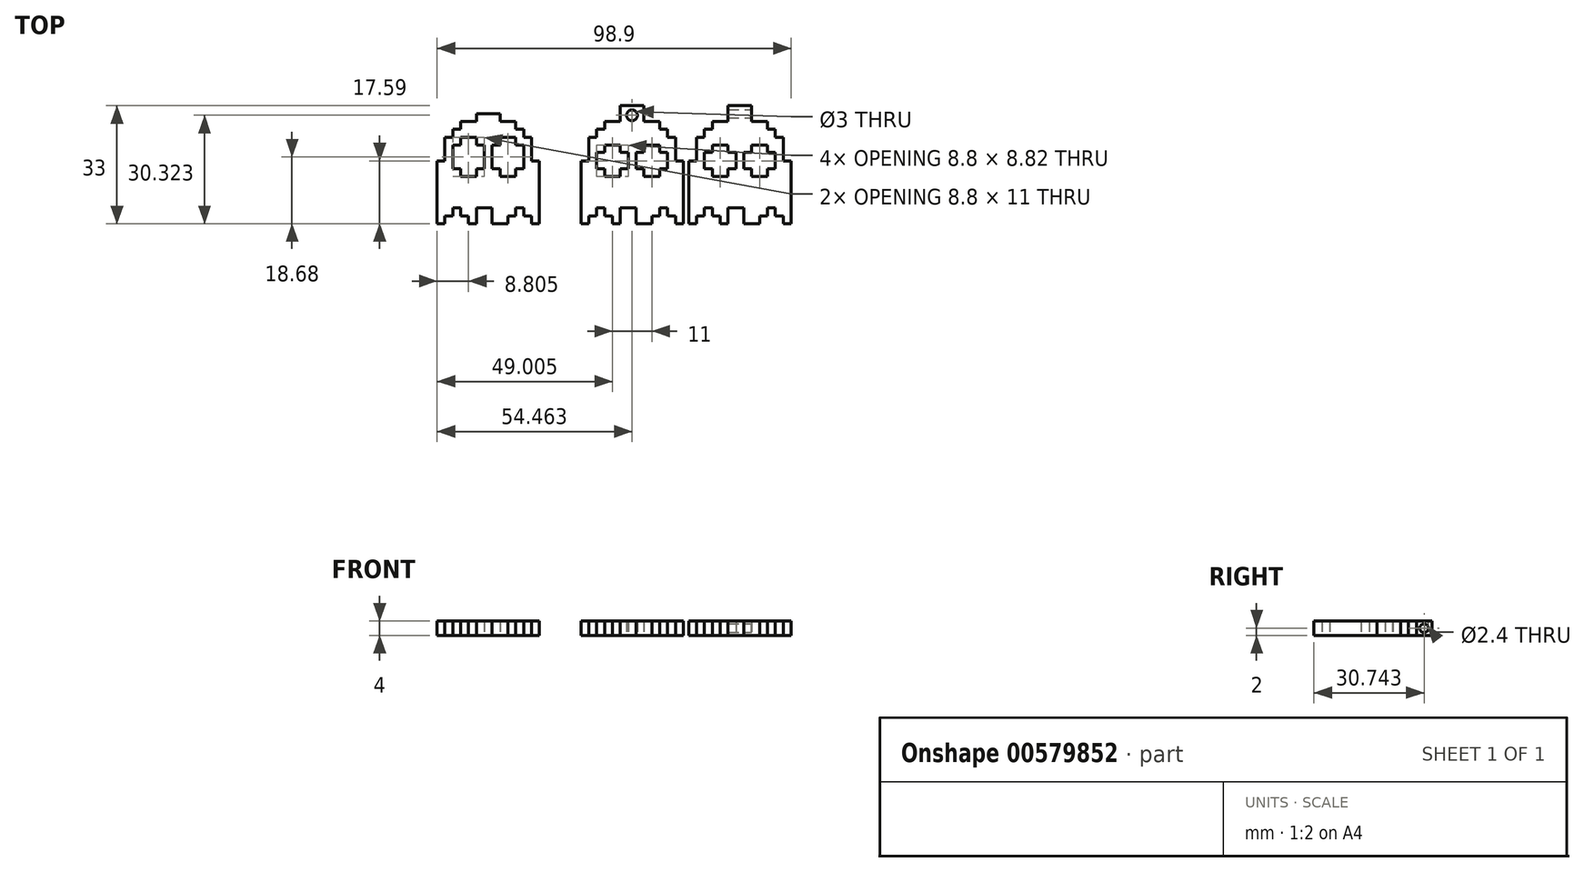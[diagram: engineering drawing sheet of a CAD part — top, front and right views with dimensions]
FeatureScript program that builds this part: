
annotation { "Feature Type Name" : "Feature", "Feature Type Description" : "" }
export const myFeature = defineFeature(function(context is Context, id is Id, definition is map)
    precondition{}
    {
        {
            var Q0;
            Q0=qCreatedBy(makeId("Top.planeOp"),FACE);
            var sketch = newSketch(context, id + "F0", { "sketchPlane" : qUnion([Q0])});
            skLineSegment(sketch, "E0.2.0.0", {"start": v(-51.84, 43.44) * mm, "end": v(-51.84, 41.24) * mm});
            skLineSegment(sketch, "E0.3.0.0", {"start": v(-49.64, 45.64) * mm, "end": v(-49.64, 43.44) * mm});
            skLineSegment(sketch, "E0.10.0.0", {"start": v(-34.24, 45.64) * mm, "end": v(-34.24, 43.44) * mm});
            skLineSegment(sketch, "E0.11.0.0", {"start": v(-32.04, 43.44) * mm, "end": v(-32.04, 41.24) * mm});
            skLineSegment(sketch, "E0.12.0.0", {"start": v(-29.84, 41.24) * mm, "end": v(-29.84, 34.64) * mm});
            skLineSegment(sketch, "E0.direction1", {"start": v(-56.24, 17.04) * mm, "end": v(-54.04, 17.04) * mm, "construction": true});
            skLineSegment(sketch, "E1.0.2.0", {"start": v(-54.04, 41.24) * mm, "end": v(-51.84, 41.24) * mm});
            skLineSegment(sketch, "E1.0.5.0", {"start": v(-56.24, 34.64) * mm, "end": v(-54.04, 34.64) * mm});
            skLineSegment(sketch, "E1.0.12.0", {"start": v(-54.04, 19.24) * mm, "end": v(-51.84, 19.24) * mm});
            skLineSegment(sketch, "E1.0.13.0", {"start": v(-56.24, 17.04) * mm, "end": v(-54.04, 17.04) * mm});
            skLineSegment(sketch, "E2.trimOffspring", {"start": v(-56.24, 34.64) * mm, "end": v(-56.24, 17.04) * mm});
            skLineSegment(sketch, "E3.trimOffspring", {"start": v(-54.04, 41.24) * mm, "end": v(-54.04, 34.64) * mm});
            skLineSegment(sketch, "E4.trimOffspring", {"start": v(-51.84, 43.44) * mm, "end": v(-49.64, 43.44) * mm});
            skLineSegment(sketch, "E5.trimOffspring", {"start": v(-49.64, 45.64) * mm, "end": v(-45.24, 45.64) * mm, "construction": true});
            skLineSegment(sketch, "E6.trimOffspring", {"start": v(-49.64, 45.64) * mm, "end": v(-45.24, 45.64) * mm});
            skLineSegment(sketch, "E7.trimOffspring", {"start": v(-36.44, 45.64) * mm, "end": v(-34.24, 45.64) * mm, "construction": true});
            skLineSegment(sketch, "E8.1.0.0", {"start": v(-27.64, 34.64) * mm, "end": v(-27.64, 17.04) * mm});
            skLineSegment(sketch, "E8.direction1", {"start": v(-29.84, 17.04) * mm, "end": v(-27.64, 17.04) * mm});
            skLineSegment(sketch, "E9", {"start": v(-29.84, 34.64) * mm, "end": v(-27.64, 34.64) * mm});
            skLineSegment(sketch, "E10.trimOffspring", {"start": v(-32.04, 19.24) * mm, "end": v(-29.84, 19.24) * mm});
            skLineSegment(sketch, "E11.trimOffspring", {"start": v(-40.84, 17.04) * mm, "end": v(-36.44, 17.04) * mm});
            skLineSegment(sketch, "E12.trimOffspring", {"start": v(-47.44, 17.04) * mm, "end": v(-45.24, 17.04) * mm});
            skLineSegment(sketch, "E13.trimOffspring", {"start": v(-49.64, 19.24) * mm, "end": v(-47.44, 19.24) * mm});
            skLineSegment(sketch, "E14", {"start": v(-45.24, 45.64) * mm, "end": v(-45.24, 47.84) * mm});
            skLineSegment(sketch, "E15", {"start": v(-45.24, 47.84) * mm, "end": v(-38.64, 47.84) * mm});
            skLineSegment(sketch, "E16", {"start": v(-38.64, 47.84) * mm, "end": v(-38.64, 45.64) * mm});
            skLineSegment(sketch, "E17.trimOffspring", {"start": v(-45.24, 39.04) * mm, "end": v(-43.04, 39.04) * mm});
            skLineSegment(sketch, "E18.trimOffspring", {"start": v(-34.24, 43.44) * mm, "end": v(-32.04, 43.44) * mm});
            skLineSegment(sketch, "E19.trimOffspring", {"start": v(-32.04, 41.24) * mm, "end": v(-29.84, 41.24) * mm});
            skLineSegment(sketch, "E20.trimOffspring", {"start": v(-32.04, 39.04) * mm, "end": v(-32.04, 32.44) * mm});
            skLineSegment(sketch, "E21.trimOffspring", {"start": v(-34.24, 39.04) * mm, "end": v(-32.04, 39.04) * mm});
            skLineSegment(sketch, "E22.trimOffspring", {"start": v(-43.04, 39.04) * mm, "end": v(-43.04, 32.44) * mm});
            skLineSegment(sketch, "E23.trimOffspring", {"start": v(-49.64, 39.04) * mm, "end": v(-49.64, 39.02) * mm});
            skLineSegment(sketch, "E24.trimOffspring", {"start": v(-38.64, 39.04) * mm, "end": v(-38.64, 39.02) * mm});
            skLineSegment(sketch, "E25.trimOffspring", {"start": v(-47.44, 19.24) * mm, "end": v(-47.44, 17.04) * mm});
            skLineSegment(sketch, "E26.trimOffspring", {"start": v(-29.84, 19.24) * mm, "end": v(-29.84, 17.04) * mm});
            skLineSegment(sketch, "E27.trimOffspring", {"start": v(-32.04, 21.44) * mm, "end": v(-32.04, 19.24) * mm});
            skLineSegment(sketch, "E28.trimOffspring", {"start": v(-34.24, 21.44) * mm, "end": v(-34.24, 19.24) * mm});
            skLineSegment(sketch, "E29.trimOffspring", {"start": v(-34.24, 21.44) * mm, "end": v(-32.04, 21.44) * mm});
            skLineSegment(sketch, "E30.trimOffspring", {"start": v(-36.44, 19.24) * mm, "end": v(-36.44, 17.04) * mm});
            skLineSegment(sketch, "E31.trimOffspring", {"start": v(-36.44, 19.24) * mm, "end": v(-34.24, 19.24) * mm});
            skLineSegment(sketch, "E32.trimOffspring", {"start": v(-40.84, 21.44) * mm, "end": v(-40.84, 17.04) * mm});
            skLineSegment(sketch, "E33.trimOffspring", {"start": v(-45.24, 21.44) * mm, "end": v(-45.24, 17.04) * mm});
            skLineSegment(sketch, "E34.trimOffspring", {"start": v(-45.24, 21.44) * mm, "end": v(-40.84, 21.44) * mm});
            skLineSegment(sketch, "E35.trimOffspring", {"start": v(-49.64, 21.44) * mm, "end": v(-49.64, 19.24) * mm});
            skLineSegment(sketch, "E36.trimOffspring", {"start": v(-51.84, 21.44) * mm, "end": v(-51.84, 19.24) * mm});
            skLineSegment(sketch, "E37.trimOffspring", {"start": v(-51.84, 21.44) * mm, "end": v(-49.64, 21.44) * mm});
            skLineSegment(sketch, "E38.trimOffspring", {"start": v(-54.04, 19.24) * mm, "end": v(-54.04, 17.04) * mm});
            skLineSegment(sketch, "E39.trimOffspring", {"start": v(-34.24, 32.44) * mm, "end": v(-32.04, 32.44) * mm});
            skLineSegment(sketch, "E40.trimOffspring", {"start": v(-38.64, 45.64) * mm, "end": v(-34.24, 45.64) * mm});
            skLineSegment(sketch, "E41", {"start": v(-34.24, 39.04) * mm, "end": v(-34.24, 39.02) * mm});
            skPoint(sketch, "E41.endSnap0", {"position": v(-35.34, 32.44) * mm});
            skLineSegment(sketch, "E42", {"start": v(-49.64, 41.24) * mm, "end": v(-49.64, 39.04) * mm});
            skLineSegment(sketch, "E43", {"start": v(-49.64, 39.04) * mm, "end": v(-51.84, 39.04) * mm});
            skLineSegment(sketch, "E44", {"start": v(-51.84, 39.04) * mm, "end": v(-51.84, 32.44) * mm});
            skLineSegment(sketch, "E45", {"start": v(-51.84, 32.44) * mm, "end": v(-51.84, 32.42) * mm});
            skLineSegment(sketch, "E46", {"start": v(-49.64, 30.22) * mm, "end": v(-45.24, 30.22) * mm});
            skLineSegment(sketch, "E47", {"start": v(-32.04, 32.42) * mm, "end": v(-32.04, 32.44) * mm});
            skLineSegment(sketch, "E48.0.1.0", {"start": v(-51.84, 32.42) * mm, "end": v(-49.64, 32.42) * mm});
            skLineSegment(sketch, "E48.0.4.0", {"start": v(-51.84, 39.02) * mm, "end": v(-49.64, 39.02) * mm});
            skLineSegment(sketch, "E48.0.5.0", {"start": v(-49.64, 41.22) * mm, "end": v(-45.24, 41.22) * mm});
            skLineSegment(sketch, "E49", {"start": v(-49.64, 32.44) * mm, "end": v(-49.64, 30.22) * mm});
            skLineSegment(sketch, "E50", {"start": v(-45.24, 30.22) * mm, "end": v(-45.24, 32.44) * mm});
            skLineSegment(sketch, "E51", {"start": v(-45.24, 39.04) * mm, "end": v(-45.24, 41.22) * mm});
            skLineSegment(sketch, "E52", {"start": v(-38.64, 32.44) * mm, "end": v(-38.64, 30.22) * mm});
            skLineSegment(sketch, "E53", {"start": v(-34.24, 32.44) * mm, "end": v(-34.24, 30.22) * mm});
            skLineSegment(sketch, "E54", {"start": v(-34.24, 39.04) * mm, "end": v(-34.24, 41.24) * mm});
            skLineSegment(sketch, "E55", {"start": v(-38.64, 39.04) * mm, "end": v(-38.64, 41.22) * mm});
            skLineSegment(sketch, "E56", {"start": v(-40.84, 32.42) * mm, "end": v(-40.84, 39.02) * mm});
            skLineSegment(sketch, "E57.trimOffspring", {"start": v(-38.64, 41.22) * mm, "end": v(-34.24, 41.22) * mm});
            skPoint(sketch, "E58.orphan", {"position": v(-32.04, 30.22) * mm});
            skLineSegment(sketch, "E59.trimOffspring", {"start": v(-40.84, 32.42) * mm, "end": v(-38.64, 32.42) * mm});
            skLineSegment(sketch, "E60.trimOffspring", {"start": v(-40.84, 39.02) * mm, "end": v(-38.64, 39.02) * mm});
            skLineSegment(sketch, "E61.trimOffspring", {"start": v(-38.64, 30.22) * mm, "end": v(-34.24, 30.22) * mm});
            skLineSegment(sketch, "E62.trimOffspring", {"start": v(-47.44, 39.02) * mm, "end": v(-47.44, 39.04) * mm});
            skLineSegment(sketch, "E63.trimOffspring", {"start": v(-45.24, 39.02) * mm, "end": v(-45.24, 39.04) * mm});
            skLineSegment(sketch, "E64.trimOffspring", {"start": v(-45.24, 39.02) * mm, "end": v(-43.04, 39.02) * mm});
            skLineSegment(sketch, "E65.trimOffspring", {"start": v(-45.24, 32.44) * mm, "end": v(-43.04, 32.44) * mm});
            skLineSegment(sketch, "E66.trimOffspring", {"start": v(-34.24, 32.42) * mm, "end": v(-32.04, 32.42) * mm});
            skLineSegment(sketch, "E67.trimOffspring", {"start": v(-34.24, 39.02) * mm, "end": v(-32.04, 39.02) * mm});
            skLineSegment(sketch, "E68.2.0.0", {"start": v(-11.64, 43.44) * mm, "end": v(-11.64, 41.24) * mm});
            skLineSegment(sketch, "E68.3.0.0", {"start": v(-9.44, 45.64) * mm, "end": v(-9.44, 43.44) * mm});
            skLineSegment(sketch, "E68.10.0.0", {"start": v(5.96, 45.64) * mm, "end": v(5.96, 43.44) * mm});
            skLineSegment(sketch, "E68.11.0.0", {"start": v(8.16, 43.44) * mm, "end": v(8.16, 41.24) * mm});
            skLineSegment(sketch, "E68.12.0.0", {"start": v(10.36, 41.24) * mm, "end": v(10.36, 34.64) * mm});
            skLineSegment(sketch, "E68.direction1", {"start": v(-16.04, 17.04) * mm, "end": v(-13.84, 17.04) * mm, "construction": true});
            skLineSegment(sketch, "E69.0.2.0", {"start": v(-13.84, 41.24) * mm, "end": v(-11.64, 41.24) * mm});
            skLineSegment(sketch, "E69.0.5.0", {"start": v(-16.04, 34.64) * mm, "end": v(-13.84, 34.64) * mm});
            skLineSegment(sketch, "E69.0.12.0", {"start": v(-13.84, 19.24) * mm, "end": v(-11.64, 19.24) * mm});
            skLineSegment(sketch, "E69.0.13.0", {"start": v(-16.04, 17.04) * mm, "end": v(-13.84, 17.04) * mm});
            skLineSegment(sketch, "E70.trimOffspring", {"start": v(-16.04, 34.64) * mm, "end": v(-16.04, 17.04) * mm});
            skLineSegment(sketch, "E71.trimOffspring", {"start": v(-13.84, 41.24) * mm, "end": v(-13.84, 34.64) * mm});
            skLineSegment(sketch, "E72.trimOffspring", {"start": v(-11.64, 43.44) * mm, "end": v(-9.44, 43.44) * mm});
            skLineSegment(sketch, "E73.trimOffspring", {"start": v(-9.44, 45.64) * mm, "end": v(-5.04, 45.64) * mm, "construction": true});
            skLineSegment(sketch, "E74.trimOffspring", {"start": v(-9.44, 45.64) * mm, "end": v(-5.04, 45.64) * mm});
            skLineSegment(sketch, "E75.trimOffspring", {"start": v(3.76, 45.64) * mm, "end": v(5.96, 45.64) * mm, "construction": true});
            skLineSegment(sketch, "E76.1.0.0", {"start": v(12.56, 34.64) * mm, "end": v(12.56, 17.04) * mm});
            skLineSegment(sketch, "E76.direction1", {"start": v(10.36, 17.04) * mm, "end": v(12.56, 17.04) * mm});
            skLineSegment(sketch, "E77", {"start": v(10.36, 34.64) * mm, "end": v(12.56, 34.64) * mm});
            skLineSegment(sketch, "E78.trimOffspring", {"start": v(8.16, 19.24) * mm, "end": v(10.36, 19.24) * mm});
            skLineSegment(sketch, "E79.trimOffspring", {"start": v(-0.64, 17.04) * mm, "end": v(3.76, 17.04) * mm});
            skLineSegment(sketch, "E80.trimOffspring", {"start": v(-7.24, 17.04) * mm, "end": v(-5.04, 17.04) * mm});
            skLineSegment(sketch, "E81.trimOffspring", {"start": v(-9.44, 19.24) * mm, "end": v(-7.24, 19.24) * mm});
            skLineSegment(sketch, "E82", {"start": v(-5.04, 45.64) * mm, "end": v(-5.04, 47.84) * mm});
            skLineSegment(sketch, "E83", {"start": v(1.56, 47.84) * mm, "end": v(1.56, 45.64) * mm});
            skLineSegment(sketch, "E84.trimOffspring", {"start": v(5.96, 43.44) * mm, "end": v(8.16, 43.44) * mm});
            skLineSegment(sketch, "E85.trimOffspring", {"start": v(8.16, 41.24) * mm, "end": v(10.36, 41.24) * mm});
            skLineSegment(sketch, "E86.trimOffspring", {"start": v(8.16, 36.95) * mm, "end": v(8.16, 32.44) * mm});
            skLineSegment(sketch, "E87.trimOffspring", {"start": v(-2.84, 36.95) * mm, "end": v(-2.84, 32.44) * mm});
            skLineSegment(sketch, "E88.trimOffspring", {"start": v(-9.44, 39.04) * mm, "end": v(-9.44, 39.02) * mm});
            skLineSegment(sketch, "E89.trimOffspring", {"start": v(1.56, 39.04) * mm, "end": v(1.56, 39.02) * mm});
            skLineSegment(sketch, "E90.trimOffspring", {"start": v(-7.24, 19.24) * mm, "end": v(-7.24, 17.04) * mm});
            skLineSegment(sketch, "E91.trimOffspring", {"start": v(10.36, 19.24) * mm, "end": v(10.36, 17.04) * mm});
            skLineSegment(sketch, "E92.trimOffspring", {"start": v(8.16, 21.44) * mm, "end": v(8.16, 19.24) * mm});
            skLineSegment(sketch, "E93.trimOffspring", {"start": v(5.96, 21.44) * mm, "end": v(5.96, 19.24) * mm});
            skLineSegment(sketch, "E94.trimOffspring", {"start": v(5.96, 21.44) * mm, "end": v(8.16, 21.44) * mm});
            skLineSegment(sketch, "E95.trimOffspring", {"start": v(3.76, 19.24) * mm, "end": v(3.76, 17.04) * mm});
            skLineSegment(sketch, "E96.trimOffspring", {"start": v(3.76, 19.24) * mm, "end": v(5.96, 19.24) * mm});
            skLineSegment(sketch, "E97.trimOffspring", {"start": v(-0.64, 21.44) * mm, "end": v(-0.64, 17.04) * mm});
            skLineSegment(sketch, "E98.trimOffspring", {"start": v(-5.04, 21.44) * mm, "end": v(-5.04, 17.04) * mm});
            skLineSegment(sketch, "E99.trimOffspring", {"start": v(-5.04, 21.44) * mm, "end": v(-0.64, 21.44) * mm});
            skLineSegment(sketch, "E100.trimOffspring", {"start": v(-9.44, 21.44) * mm, "end": v(-9.44, 19.24) * mm});
            skLineSegment(sketch, "E101.trimOffspring", {"start": v(-11.64, 21.44) * mm, "end": v(-11.64, 19.24) * mm});
            skLineSegment(sketch, "E102.trimOffspring", {"start": v(-11.64, 21.44) * mm, "end": v(-9.44, 21.44) * mm});
            skLineSegment(sketch, "E103.trimOffspring", {"start": v(-13.84, 19.24) * mm, "end": v(-13.84, 17.04) * mm});
            skLineSegment(sketch, "E104.trimOffspring", {"start": v(5.96, 32.44) * mm, "end": v(8.16, 32.44) * mm});
            skLineSegment(sketch, "E105.trimOffspring", {"start": v(1.56, 45.64) * mm, "end": v(5.96, 45.64) * mm});
            skLineSegment(sketch, "E106", {"start": v(5.96, 39.04) * mm, "end": v(5.96, 39.02) * mm});
            skLineSegment(sketch, "E107", {"start": v(-9.44, 41.24) * mm, "end": v(-9.44, 41.22) * mm});
            skLineSegment(sketch, "E108", {"start": v(-11.64, 36.95) * mm, "end": v(-11.64, 32.44) * mm});
            skLineSegment(sketch, "E109", {"start": v(-11.64, 32.44) * mm, "end": v(-11.64, 32.42) * mm});
            skLineSegment(sketch, "E110", {"start": v(-9.44, 30.22) * mm, "end": v(-5.04, 30.22) * mm});
            skLineSegment(sketch, "E111", {"start": v(8.16, 32.42) * mm, "end": v(8.16, 32.44) * mm});
            skLineSegment(sketch, "E112.0.1.0", {"start": v(-11.64, 32.42) * mm, "end": v(-9.44, 32.42) * mm});
            skLineSegment(sketch, "E113", {"start": v(-9.44, 32.44) * mm, "end": v(-9.44, 30.22) * mm});
            skLineSegment(sketch, "E114", {"start": v(-5.04, 30.22) * mm, "end": v(-5.04, 32.44) * mm});
            skLineSegment(sketch, "E115", {"start": v(1.56, 32.44) * mm, "end": v(1.56, 30.22) * mm});
            skLineSegment(sketch, "E116", {"start": v(5.96, 32.44) * mm, "end": v(5.96, 30.22) * mm});
            skLineSegment(sketch, "E117", {"start": v(-0.64, 32.42) * mm, "end": v(-0.64, 36.95) * mm});
            skLineSegment(sketch, "E118.trimOffspring", {"start": v(-0.64, 32.42) * mm, "end": v(1.56, 32.42) * mm});
            skLineSegment(sketch, "E119.trimOffspring", {"start": v(1.56, 30.22) * mm, "end": v(5.96, 30.22) * mm});
            skLineSegment(sketch, "E120.trimOffspring", {"start": v(-7.24, 39.02) * mm, "end": v(-7.24, 39.04) * mm});
            skLineSegment(sketch, "E121.trimOffspring", {"start": v(-5.04, 39.02) * mm, "end": v(-5.04, 39.04) * mm});
            skLineSegment(sketch, "E122.trimOffspring", {"start": v(-5.04, 32.44) * mm, "end": v(-2.84, 32.44) * mm});
            skLineSegment(sketch, "E123.trimOffspring", {"start": v(5.96, 32.42) * mm, "end": v(8.16, 32.42) * mm});
            skLineSegment(sketch, "E124", {"start": v(-9.44, 39.04) * mm, "end": v(-5.04, 39.04) * mm});
            skLineSegment(sketch, "E125", {"start": v(1.56, 39.04) * mm, "end": v(5.96, 39.04) * mm});
            skLineSegment(sketch, "E126", {"start": v(-11.64, 36.95) * mm, "end": v(-9.44, 36.95) * mm});
            skLineSegment(sketch, "E127", {"start": v(-9.44, 39.04) * mm, "end": v(-9.44, 36.95) * mm});
            skLineSegment(sketch, "E128", {"start": v(-5.04, 39.04) * mm, "end": v(-5.04, 36.95) * mm});
            skLineSegment(sketch, "E129", {"start": v(1.56, 39.04) * mm, "end": v(1.56, 36.95) * mm});
            skLineSegment(sketch, "E130", {"start": v(5.96, 39.04) * mm, "end": v(5.96, 36.95) * mm});
            skLineSegment(sketch, "E131.trimOffspring", {"start": v(-0.64, 36.95) * mm, "end": v(1.56, 36.95) * mm});
            skLineSegment(sketch, "E132", {"start": v(-5.04, 36.95) * mm, "end": v(-2.84, 36.95) * mm});
            skLineSegment(sketch, "E133.trimOffspring", {"start": v(5.96, 36.95) * mm, "end": v(8.16, 36.95) * mm});
            skLineSegment(sketch, "E134", {"start": v(-5.04, 47.84) * mm, "end": v(-5.04, 50.04) * mm});
            skLineSegment(sketch, "E135", {"start": v(-5.04, 50.04) * mm, "end": v(1.56, 50.04) * mm});
            skLineSegment(sketch, "E136", {"start": v(1.56, 50.04) * mm, "end": v(1.56, 47.84) * mm});
            skCircle(sketch, "E137", {"center": v(-1.78, 47.36) * mm, "radius": 1.5 * mm});
            skLineSegment(sketch, "E138.2.0.0", {"start": v(18.46, 43.44) * mm, "end": v(18.46, 41.24) * mm});
            skLineSegment(sketch, "E138.3.0.0", {"start": v(20.66, 45.64) * mm, "end": v(20.66, 43.44) * mm});
            skLineSegment(sketch, "E138.10.0.0", {"start": v(36.06, 45.64) * mm, "end": v(36.06, 43.44) * mm});
            skLineSegment(sketch, "E138.11.0.0", {"start": v(38.26, 43.44) * mm, "end": v(38.26, 41.24) * mm});
            skLineSegment(sketch, "E138.12.0.0", {"start": v(40.46, 41.24) * mm, "end": v(40.46, 34.64) * mm});
            skLineSegment(sketch, "E138.direction1", {"start": v(14.06, 17.04) * mm, "end": v(16.26, 17.04) * mm, "construction": true});
            skLineSegment(sketch, "E139.0.2.0", {"start": v(16.26, 41.24) * mm, "end": v(18.46, 41.24) * mm});
            skLineSegment(sketch, "E139.0.5.0", {"start": v(14.06, 34.64) * mm, "end": v(16.26, 34.64) * mm});
            skLineSegment(sketch, "E139.0.12.0", {"start": v(16.26, 19.24) * mm, "end": v(18.46, 19.24) * mm});
            skLineSegment(sketch, "E139.0.13.0", {"start": v(14.06, 17.04) * mm, "end": v(16.26, 17.04) * mm});
            skLineSegment(sketch, "E140.trimOffspring", {"start": v(14.06, 34.64) * mm, "end": v(14.06, 17.04) * mm});
            skLineSegment(sketch, "E141.trimOffspring", {"start": v(16.26, 41.24) * mm, "end": v(16.26, 34.64) * mm});
            skLineSegment(sketch, "E142.trimOffspring", {"start": v(18.46, 43.44) * mm, "end": v(20.66, 43.44) * mm});
            skLineSegment(sketch, "E143.trimOffspring", {"start": v(20.66, 45.64) * mm, "end": v(25.06, 45.64) * mm, "construction": true});
            skLineSegment(sketch, "E144.trimOffspring", {"start": v(20.66, 45.64) * mm, "end": v(25.06, 45.64) * mm});
            skLineSegment(sketch, "E145.trimOffspring", {"start": v(33.86, 45.64) * mm, "end": v(36.06, 45.64) * mm, "construction": true});
            skLineSegment(sketch, "E146.1.0.0", {"start": v(42.66, 34.64) * mm, "end": v(42.66, 17.04) * mm});
            skLineSegment(sketch, "E146.direction1", {"start": v(40.46, 17.04) * mm, "end": v(42.66, 17.04) * mm});
            skLineSegment(sketch, "E147", {"start": v(40.46, 34.64) * mm, "end": v(42.66, 34.64) * mm});
            skLineSegment(sketch, "E148.trimOffspring", {"start": v(38.26, 19.24) * mm, "end": v(40.46, 19.24) * mm});
            skLineSegment(sketch, "E149.trimOffspring", {"start": v(29.46, 17.04) * mm, "end": v(33.86, 17.04) * mm});
            skLineSegment(sketch, "E150.trimOffspring", {"start": v(22.86, 17.04) * mm, "end": v(25.06, 17.04) * mm});
            skLineSegment(sketch, "E151.trimOffspring", {"start": v(20.66, 19.24) * mm, "end": v(22.86, 19.24) * mm});
            skLineSegment(sketch, "E152", {"start": v(25.06, 45.64) * mm, "end": v(25.06, 47.84) * mm});
            skLineSegment(sketch, "E153", {"start": v(31.66, 47.84) * mm, "end": v(31.66, 45.64) * mm});
            skLineSegment(sketch, "E154.trimOffspring", {"start": v(36.06, 43.44) * mm, "end": v(38.26, 43.44) * mm});
            skLineSegment(sketch, "E155.trimOffspring", {"start": v(38.26, 41.24) * mm, "end": v(40.46, 41.24) * mm});
            skLineSegment(sketch, "E156.trimOffspring", {"start": v(38.26, 36.95) * mm, "end": v(38.26, 32.44) * mm});
            skLineSegment(sketch, "E157.trimOffspring", {"start": v(27.26, 36.95) * mm, "end": v(27.26, 32.44) * mm});
            skLineSegment(sketch, "E158.trimOffspring", {"start": v(20.66, 39.04) * mm, "end": v(20.66, 39.02) * mm});
            skLineSegment(sketch, "E159.trimOffspring", {"start": v(31.66, 39.04) * mm, "end": v(31.66, 39.02) * mm});
            skLineSegment(sketch, "E160.trimOffspring", {"start": v(22.86, 19.24) * mm, "end": v(22.86, 17.04) * mm});
            skLineSegment(sketch, "E161.trimOffspring", {"start": v(40.46, 19.24) * mm, "end": v(40.46, 17.04) * mm});
            skLineSegment(sketch, "E162.trimOffspring", {"start": v(38.26, 21.44) * mm, "end": v(38.26, 19.24) * mm});
            skLineSegment(sketch, "E163.trimOffspring", {"start": v(36.06, 21.44) * mm, "end": v(36.06, 19.24) * mm});
            skLineSegment(sketch, "E164.trimOffspring", {"start": v(36.06, 21.44) * mm, "end": v(38.26, 21.44) * mm});
            skLineSegment(sketch, "E165.trimOffspring", {"start": v(33.86, 19.24) * mm, "end": v(33.86, 17.04) * mm});
            skLineSegment(sketch, "E166.trimOffspring", {"start": v(33.86, 19.24) * mm, "end": v(36.06, 19.24) * mm});
            skLineSegment(sketch, "E167.trimOffspring", {"start": v(29.46, 21.44) * mm, "end": v(29.46, 17.04) * mm});
            skLineSegment(sketch, "E168.trimOffspring", {"start": v(25.06, 21.44) * mm, "end": v(25.06, 17.04) * mm});
            skLineSegment(sketch, "E169.trimOffspring", {"start": v(25.06, 21.44) * mm, "end": v(29.46, 21.44) * mm});
            skLineSegment(sketch, "E170.trimOffspring", {"start": v(20.66, 21.44) * mm, "end": v(20.66, 19.24) * mm});
            skLineSegment(sketch, "E171.trimOffspring", {"start": v(18.46, 21.44) * mm, "end": v(18.46, 19.24) * mm});
            skLineSegment(sketch, "E172.trimOffspring", {"start": v(18.46, 21.44) * mm, "end": v(20.66, 21.44) * mm});
            skLineSegment(sketch, "E173.trimOffspring", {"start": v(16.26, 19.24) * mm, "end": v(16.26, 17.04) * mm});
            skLineSegment(sketch, "E174.trimOffspring", {"start": v(36.06, 32.44) * mm, "end": v(38.26, 32.44) * mm});
            skLineSegment(sketch, "E175.trimOffspring", {"start": v(31.66, 45.64) * mm, "end": v(36.06, 45.64) * mm});
            skLineSegment(sketch, "E176", {"start": v(36.06, 39.04) * mm, "end": v(36.06, 39.02) * mm});
            skLineSegment(sketch, "E177", {"start": v(20.66, 41.24) * mm, "end": v(20.66, 41.22) * mm});
            skLineSegment(sketch, "E178", {"start": v(18.46, 36.95) * mm, "end": v(18.46, 32.44) * mm});
            skLineSegment(sketch, "E179", {"start": v(18.46, 32.44) * mm, "end": v(18.46, 32.42) * mm});
            skLineSegment(sketch, "E180", {"start": v(20.66, 30.22) * mm, "end": v(25.06, 30.22) * mm});
            skLineSegment(sketch, "E181", {"start": v(38.26, 32.42) * mm, "end": v(38.26, 32.44) * mm});
            skLineSegment(sketch, "E182.0.1.0", {"start": v(18.46, 32.42) * mm, "end": v(20.66, 32.42) * mm});
            skLineSegment(sketch, "E183", {"start": v(20.66, 32.44) * mm, "end": v(20.66, 30.22) * mm});
            skLineSegment(sketch, "E184", {"start": v(25.06, 30.22) * mm, "end": v(25.06, 32.44) * mm});
            skLineSegment(sketch, "E185", {"start": v(31.66, 32.44) * mm, "end": v(31.66, 30.22) * mm});
            skLineSegment(sketch, "E186", {"start": v(36.06, 32.44) * mm, "end": v(36.06, 30.22) * mm});
            skLineSegment(sketch, "E187", {"start": v(29.46, 32.42) * mm, "end": v(29.46, 36.95) * mm});
            skLineSegment(sketch, "E188.trimOffspring", {"start": v(29.46, 32.42) * mm, "end": v(31.66, 32.42) * mm});
            skLineSegment(sketch, "E189.trimOffspring", {"start": v(31.66, 30.22) * mm, "end": v(36.06, 30.22) * mm});
            skLineSegment(sketch, "E190.trimOffspring", {"start": v(22.86, 39.02) * mm, "end": v(22.86, 39.04) * mm});
            skLineSegment(sketch, "E191.trimOffspring", {"start": v(25.06, 39.02) * mm, "end": v(25.06, 39.04) * mm});
            skLineSegment(sketch, "E192.trimOffspring", {"start": v(25.06, 32.44) * mm, "end": v(27.26, 32.44) * mm});
            skLineSegment(sketch, "E193.trimOffspring", {"start": v(36.06, 32.42) * mm, "end": v(38.26, 32.42) * mm});
            skLineSegment(sketch, "E194", {"start": v(20.66, 39.04) * mm, "end": v(25.06, 39.04) * mm});
            skLineSegment(sketch, "E195", {"start": v(31.66, 39.04) * mm, "end": v(36.06, 39.04) * mm});
            skLineSegment(sketch, "E196", {"start": v(18.46, 36.95) * mm, "end": v(20.66, 36.95) * mm});
            skLineSegment(sketch, "E197", {"start": v(20.66, 39.04) * mm, "end": v(20.66, 36.95) * mm});
            skLineSegment(sketch, "E198", {"start": v(25.06, 39.04) * mm, "end": v(25.06, 36.95) * mm});
            skLineSegment(sketch, "E199", {"start": v(31.66, 39.04) * mm, "end": v(31.66, 36.95) * mm});
            skLineSegment(sketch, "E200", {"start": v(36.06, 39.04) * mm, "end": v(36.06, 36.95) * mm});
            skLineSegment(sketch, "E201.trimOffspring", {"start": v(29.46, 36.95) * mm, "end": v(31.66, 36.95) * mm});
            skLineSegment(sketch, "E202", {"start": v(25.06, 36.95) * mm, "end": v(27.26, 36.95) * mm});
            skLineSegment(sketch, "E203.trimOffspring", {"start": v(36.06, 36.95) * mm, "end": v(38.26, 36.95) * mm});
            skLineSegment(sketch, "E204", {"start": v(25.06, 47.84) * mm, "end": v(25.06, 50.04) * mm});
            skLineSegment(sketch, "E205", {"start": v(25.06, 50.04) * mm, "end": v(31.66, 50.04) * mm});
            skLineSegment(sketch, "E206", {"start": v(31.66, 50.04) * mm, "end": v(31.66, 47.84) * mm});
            skSolve(sketch);
        }
        {
            var Q0;
            Q0=qSketchRegion(id+"F0",true);
            extrude(context, id + "F1", {"entities" : qUnion([Q0]), "depth" : 4 * mm, "offsetDistance" : 25 * mm});
        }
        {
            var Q0;
            Q0=makeQuery(id+"F1.opExtrude","SWEPT_FACE",FACE,{"disambiguationData":[OSD([sQuery(id+"F0.wireOp",EDGE,"E153"),sQuery(id+"F0.wireOp",EDGE,"E206")])]});
            var sketch = newSketch(context, id + "F2", { "sketchPlane" : qUnion([Q0])});
            skCircle(sketch, "E207", {"center": v(47.78, 2) * mm, "radius": 1.2 * mm});
            skPoint(sketch, "E207.centerSnap0", {"position": v(45.64, 2) * mm});
            skSolve(sketch);
        }
        {
            var Q0;
            Q0=makeQuery(id+"F2.imprint","IMPRINT",FACE,{"disambiguationData":[TD([[makeQuery(id+"F2.imprint","IMPRINT",EDGE,{"derivedFrom":sQuery(id+"F2.wireOp",EDGE,"E207")}),1.0]])]});
            extrude(context, id + "F3", {"entities" : qUnion([Q0]), "operationType" : NewBodyOperationType.REMOVE, "endBound" : BoundingType.UP_TO_NEXT, "oppositeDirection" : true, "depth" : 25 * mm, "offsetDistance" : 25 * mm});
        }
    });
